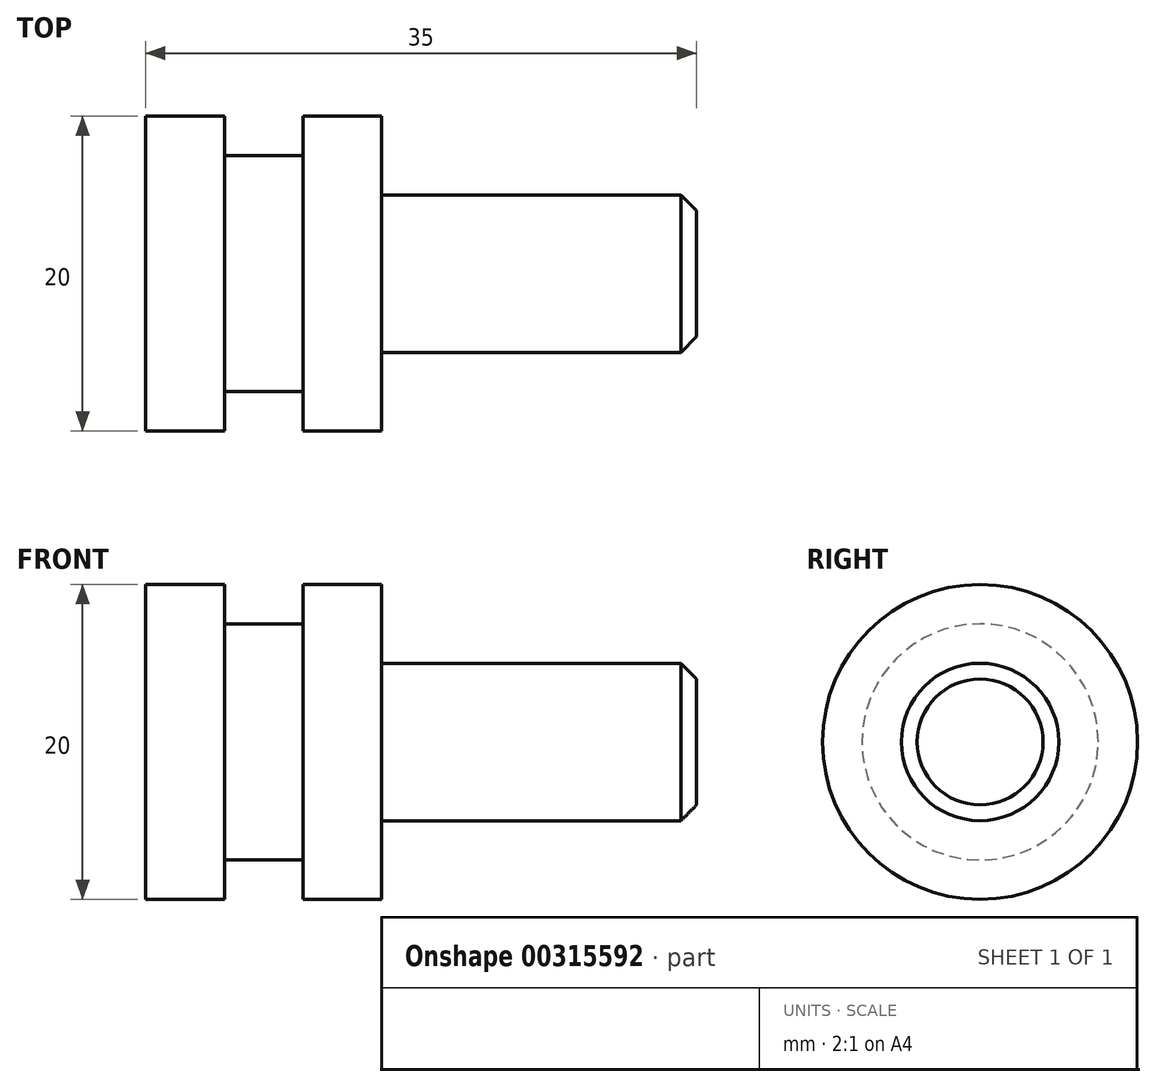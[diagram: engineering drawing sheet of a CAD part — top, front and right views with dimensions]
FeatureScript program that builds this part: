
annotation { "Feature Type Name" : "Feature", "Feature Type Description" : "" }
export const myFeature = defineFeature(function(context is Context, id is Id, definition is map)
    precondition{}
    {
        {
            var Q0;
            Q0=qCreatedBy(makeId("Right.planeOp"),FACE);
            var sketch = newSketch(context, id + "F0", { "sketchPlane" : qUnion([Q0])});
            skCircle(sketch, "E0", {"center": v(0, 0) * mm, "radius": 10 * mm});
            skSolve(sketch);
        }
        {
            var Q0;
            Q0=makeQuery(id+"F0.imprint","IMPRINT",FACE,{"disambiguationData":[TD([[makeQuery(id+"F0.imprint","IMPRINT",EDGE,{"derivedFrom":sQuery(id+"F0.wireOp",EDGE,"E0")}),1.0]])]});
            extrude(context, id + "F1", {"entities" : qUnion([Q0]), "depth" : 5 * mm});
        }
        {
            var Q0;
            Q0=makeQuery(id+"F1.opExtrude","CAP_FACE",FACE,{"disambiguationData":[OSD([sQuery(id+"F0.wireOp",EDGE,"E0")])],"isStart":false});
            var sketch = newSketch(context, id + "F2", { "sketchPlane" : qUnion([Q0])});
            skCircle(sketch, "E1", {"center": v(0, 0) * mm, "radius": 7.5 * mm});
            skSolve(sketch);
        }
        {
            var Q0;
            Q0 = qSketchRegion(id + "F2", true);
            extrude(context, id + "F3", {"entities" : qUnion([Q0]), "operationType" : NewBodyOperationType.ADD, "depth" : 5 * mm});
        }
        {
            var Q0;
            Q0=makeQuery(id+"F3.opExtrude","CAP_FACE",FACE,{"disambiguationData":[OSD([sQuery(id+"F2.wireOp",EDGE,"E1")])],"isStart":false});
            var sketch = newSketch(context, id + "F4", { "sketchPlane" : qUnion([Q0])});
            skCircle(sketch, "E2", {"center": v(0, 0) * mm, "radius": 10 * mm});
            skSolve(sketch);
        }
        {
            var Q0;
            Q0 = qSketchRegion(id + "F4", true);
            extrude(context, id + "F5", {"entities" : qUnion([Q0]), "operationType" : NewBodyOperationType.ADD, "depth" : 5 * mm});
        }
        {
            var Q0;
            Q0=makeQuery(id+"F5.opExtrude","CAP_FACE",FACE,{"disambiguationData":[OSD([sQuery(id+"F4.wireOp",EDGE,"E2")])],"isStart":false});
            var sketch = newSketch(context, id + "F6", { "sketchPlane" : qUnion([Q0])});
            skCircle(sketch, "E3", {"center": v(0, 0) * mm, "radius": 5 * mm});
            skSolve(sketch);
        }
        {
            var Q0;
            Q0 = qSketchRegion(id + "F6", true);
            extrude(context, id + "F7", {"entities" : qUnion([Q0]), "operationType" : NewBodyOperationType.ADD, "depth" : 20 * mm});
        }
        {
            var Q0;
            Q0=makeQuery(id+"F7.opExtrude","CAP_EDGE",EDGE,{"disambiguationData":[OSD([sQuery(id+"F6.wireOp",EDGE,"E3")])],"isStart":false});
            chamfer(context, id + "F8", {"entities" : qUnion([Q0]), "width" : 1 * mm, "tangentPropagation" : true});
        }
    });
